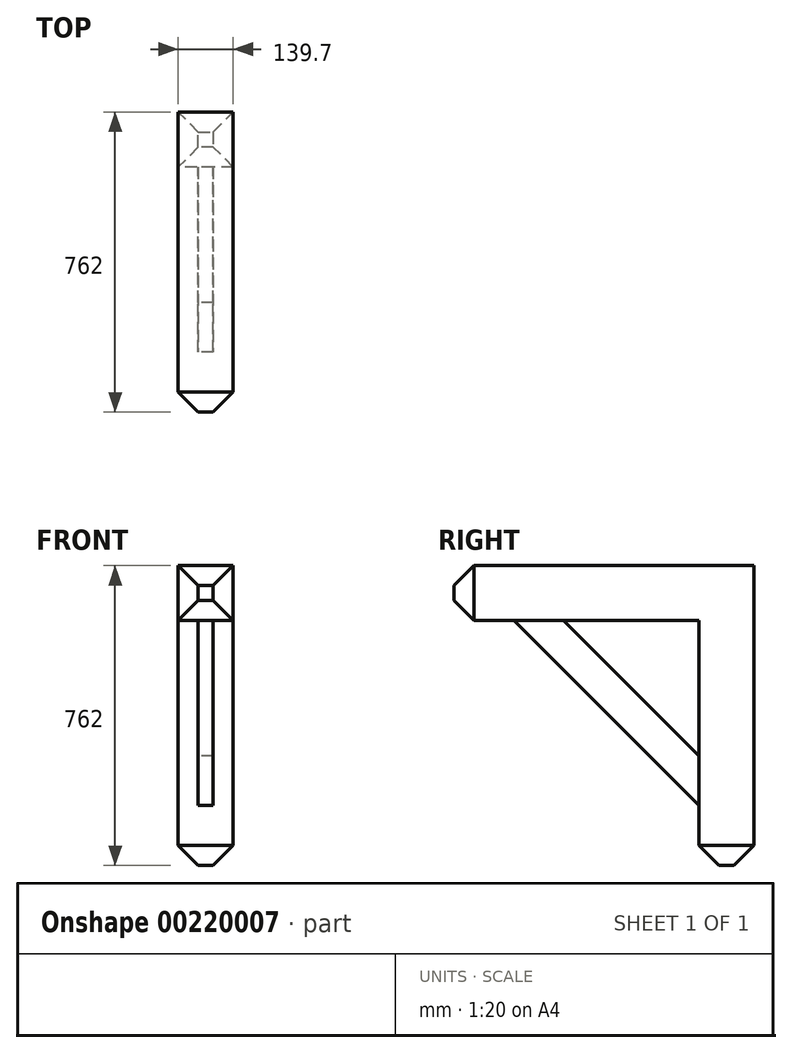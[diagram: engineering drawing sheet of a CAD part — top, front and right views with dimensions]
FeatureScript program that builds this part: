
annotation { "Feature Type Name" : "Feature", "Feature Type Description" : "" }
export const myFeature = defineFeature(function(context is Context, id is Id, definition is map)
    precondition{}
    {
        {
            var Q0;
            Q0=qCreatedBy(makeId("Right.planeOp"),FACE);
            var sketch = newSketch(context, id + "F0", { "sketchPlane" : qUnion([Q0])});
            skLineSegment(sketch, "E0", {"start": v(-762, 0) * mm, "end": v(0, 0) * mm});
            skLineSegment(sketch, "E1", {"start": v(0, 0) * mm, "end": v(0, -762) * mm});
            skLineSegment(sketch, "E2", {"start": v(0, -762) * mm, "end": v(-139.7, -762) * mm});
            skLineSegment(sketch, "E3", {"start": v(-139.7, -762) * mm, "end": v(-139.7, -139.7) * mm});
            skLineSegment(sketch, "E4", {"start": v(-139.7, -139.7) * mm, "end": v(-762, -139.7) * mm});
            skLineSegment(sketch, "E5", {"start": v(-762, 0) * mm, "end": v(-762, -139.7) * mm});
            skSolve(sketch);
        }
        {
            var Q0;
            Q0=makeQuery(id+"F0.imprint","IMPRINT",FACE,{"disambiguationData":[TD([[makeQuery(id+"F0.imprint","IMPRINT",EDGE,{"derivedFrom":sQuery(id+"F0.wireOp",EDGE,"E0")}),-1.0]])]});
            extrude(context, id + "F1", {"entities" : qUnion([Q0]), "endBound" : BoundingType.SYMMETRIC, "depth" : 139.7 * mm});
        }
        {
            var Q0;
            Q0=makeQuery(id+"F1.opExtrude","SWEPT_EDGE",EDGE,{"disambiguationData":[OSD([sQuery(id+"F0.wireOp",EDGE,"E4"),sQuery(id+"F0.wireOp",EDGE,"E5")])]});
            var Q1;
            Q1=makeQuery(id+"F1.opExtrude","CAP_EDGE",EDGE,{"disambiguationData":[OSD([sQuery(id+"F0.wireOp",EDGE,"E2")])],"isStart":false});
            var Q2;
            Q2=makeQuery(id+"F1.opExtrude","SWEPT_EDGE",EDGE,{"disambiguationData":[OSD([sQuery(id+"F0.wireOp",EDGE,"E2"),sQuery(id+"F0.wireOp",EDGE,"E3")])]});
            var Q3;
            Q3=makeQuery(id+"F1.opExtrude","CAP_EDGE",EDGE,{"disambiguationData":[OSD([sQuery(id+"F0.wireOp",EDGE,"E2")])],"isStart":true});
            var Q4;
            Q4=makeQuery(id+"F1.opExtrude","SWEPT_EDGE",EDGE,{"disambiguationData":[OSD([sQuery(id+"F0.wireOp",EDGE,"E1"),sQuery(id+"F0.wireOp",EDGE,"E2")])]});
            var Q5;
            Q5=makeQuery(id+"F1.opExtrude","CAP_EDGE",EDGE,{"disambiguationData":[OSD([sQuery(id+"F0.wireOp",EDGE,"E5")])],"isStart":true});
            var Q6;
            Q6=makeQuery(id+"F1.opExtrude","SWEPT_EDGE",EDGE,{"disambiguationData":[OSD([sQuery(id+"F0.wireOp",EDGE,"E0"),sQuery(id+"F0.wireOp",EDGE,"E5")])]});
            var Q7;
            Q7=makeQuery(id+"F1.opExtrude","CAP_EDGE",EDGE,{"disambiguationData":[OSD([sQuery(id+"F0.wireOp",EDGE,"E5")])],"isStart":false});
            chamfer(context, id + "F2", {"entities" : qUnion([Q0, Q1, Q2, Q3, Q4, Q5, Q6, Q7]), "chamferType" : ChamferType.TWO_OFFSETS, "width1" : 50.8 * mm, "oppositeDirection" : false, "width2" : 50.8 * mm, "tangentPropagation" : true});
        }
        {
            var Q0;
            Q0=qCreatedBy(makeId("Right.planeOp"),FACE);
            var sketch = newSketch(context, id + "F3", { "sketchPlane" : qUnion([Q0])});
            skLineSegment(sketch, "E6", {"start": v(-609.6, -139.7) * mm, "end": v(-483.88, -139.7) * mm});
            skLineSegment(sketch, "E7", {"start": v(-483.88, -139.7) * mm, "end": v(-139.7, -483.88) * mm});
            skLineSegment(sketch, "E8", {"start": v(-139.7, -483.88) * mm, "end": v(-139.7, -609.6) * mm});
            skLineSegment(sketch, "E9", {"start": v(-139.7, -609.6) * mm, "end": v(-609.6, -139.7) * mm});
            skSolve(sketch);
        }
        {
            var Q0;
            Q0=makeQuery(id+"F3.imprint","IMPRINT",FACE,{"disambiguationData":[TD([[makeQuery(id+"F3.imprint","IMPRINT",EDGE,{"derivedFrom":sQuery(id+"F3.wireOp",EDGE,"E6")}),-1.0]])]});
            extrude(context, id + "F4", {"entities" : qUnion([Q0]), "operationType" : NewBodyOperationType.ADD, "endBound" : BoundingType.SYMMETRIC, "depth" : 38.1 * mm});
        }
    });
